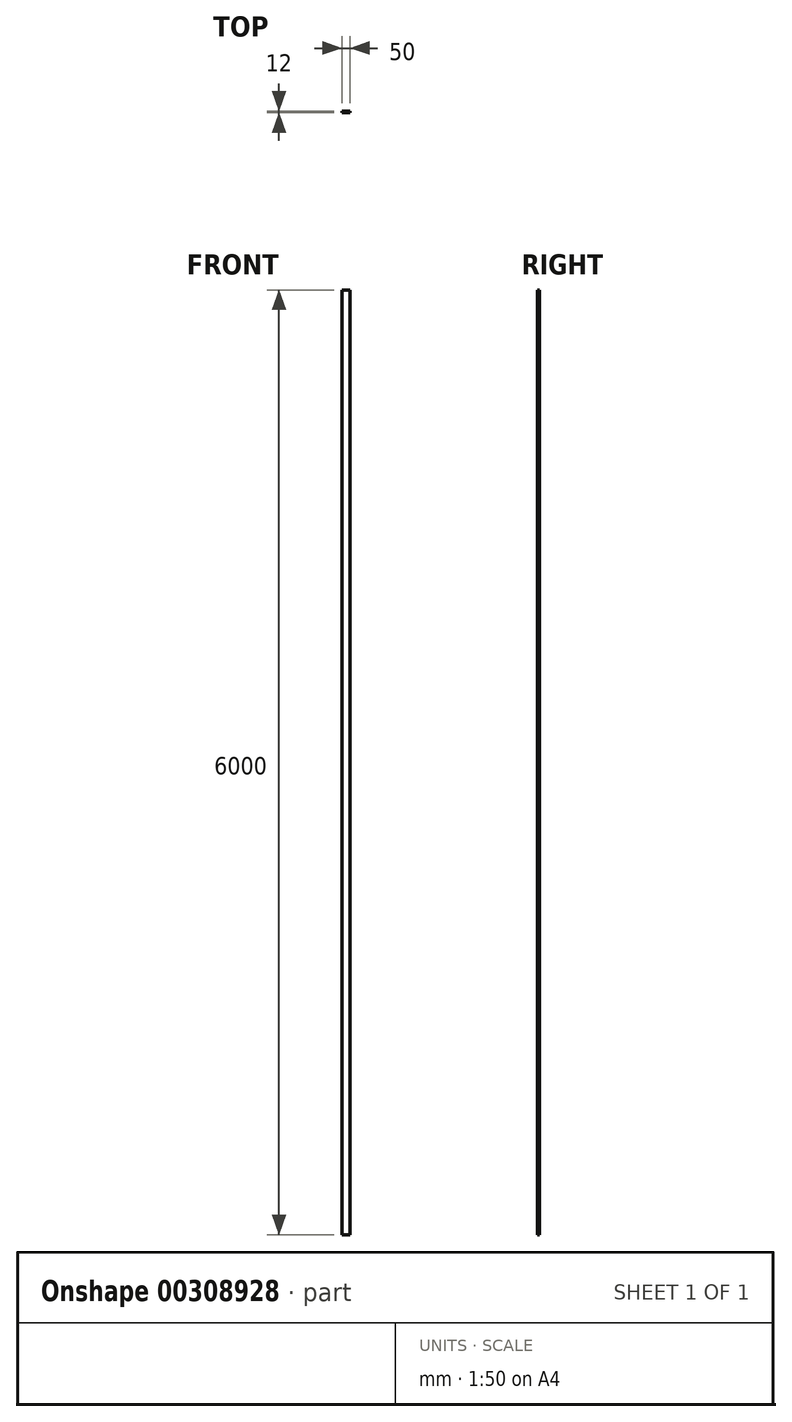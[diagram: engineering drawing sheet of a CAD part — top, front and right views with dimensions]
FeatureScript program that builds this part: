
annotation { "Feature Type Name" : "Feature", "Feature Type Description" : "" }
export const myFeature = defineFeature(function(context is Context, id is Id, definition is map)
    precondition{}
    {
        {
            var Q0;
            Q0=qCreatedBy(makeId("Top.planeOp"),FACE);
            var sketch = newSketch(context, id + "F0", { "sketchPlane" : qUnion([Q0])});
            skLineSegment(sketch, "E0.bottom", {"start": v(25, -6) * mm, "end": v(-25, -6) * mm});
            skLineSegment(sketch, "E0.top", {"start": v(25, 6) * mm, "end": v(-25, 6) * mm});
            skLineSegment(sketch, "E0.left", {"start": v(25, -6) * mm, "end": v(25, 6) * mm});
            skLineSegment(sketch, "E0.right", {"start": v(-25, -6) * mm, "end": v(-25, 6) * mm});
            skPoint(sketch, "E0.middle", {"position": v(0, 0) * mm});
            skSolve(sketch);
        }
        {
            var Q0;
            Q0 = qSketchRegion(id + "F0", true);
            extrude(context, id + "F1", {"entities" : qUnion([Q0]), "depth" : 6000 * mm});
        }
    });
